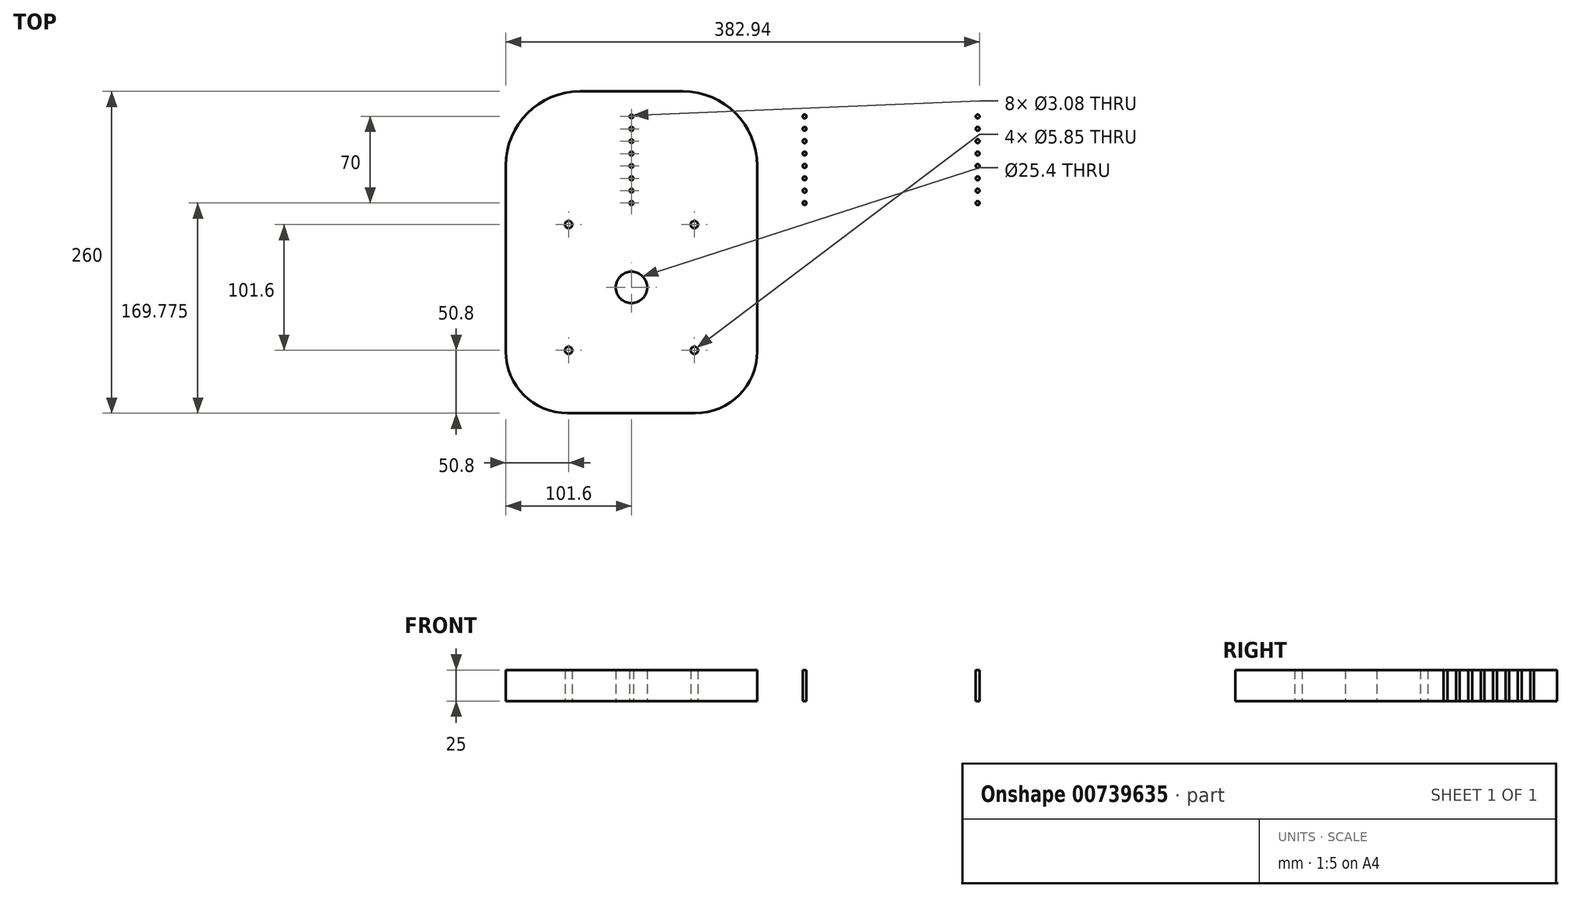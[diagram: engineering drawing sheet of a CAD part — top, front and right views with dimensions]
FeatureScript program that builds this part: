
annotation { "Feature Type Name" : "Feature", "Feature Type Description" : "" }
export const myFeature = defineFeature(function(context is Context, id is Id, definition is map)
    precondition{}
    {
        {
            var Q0;
            Q0=qCreatedBy(makeId("Top.planeOp"),FACE);
            var sketch = newSketch(context, id + "F0", { "sketchPlane" : qUnion([Q0])});
            skLineSegment(sketch, "E0.bottom", {"start": v(0, 0) * mm, "end": v(203.2, 0) * mm});
            skLineSegment(sketch, "E0.top", {"start": v(0, 260) * mm, "end": v(203.2, 260) * mm});
            skLineSegment(sketch, "E0.left", {"start": v(0, 0) * mm, "end": v(0, 260) * mm});
            skLineSegment(sketch, "E0.right", {"start": v(203.2, 0) * mm, "end": v(203.2, 260) * mm});
            skLineSegment(sketch, "E1", {"start": v(101.6, 0) * mm, "end": v(101.6, 260) * mm, "construction": true});
            skCircle(sketch, "E2", {"center": v(101.6, 239.78) * mm, "radius": 1.54 * mm});
            skCircle(sketch, "E3", {"center": v(101.6, 101.6) * mm, "radius": 12.7 * mm});
            skLineSegment(sketch, "E4.bottom", {"start": v(152.4, 152.4) * mm, "end": v(50.8, 152.4) * mm});
            skLineSegment(sketch, "E4.top", {"start": v(152.4, 50.8) * mm, "end": v(50.8, 50.8) * mm});
            skLineSegment(sketch, "E4.left", {"start": v(152.4, 152.4) * mm, "end": v(152.4, 50.8) * mm});
            skLineSegment(sketch, "E4.right", {"start": v(50.8, 152.4) * mm, "end": v(50.8, 50.8) * mm});
            skCircle(sketch, "E5", {"center": v(50.8, 152.4) * mm, "radius": 2.93 * mm});
            skCircle(sketch, "E6", {"center": v(152.4, 152.4) * mm, "radius": 2.93 * mm});
            skCircle(sketch, "E7", {"center": v(50.8, 50.8) * mm, "radius": 2.93 * mm});
            skCircle(sketch, "E8", {"center": v(152.4, 50.8) * mm, "radius": 2.93 * mm});
            skCircle(sketch, "E9.0.1.0", {"center": v(101.6, 229.78) * mm, "radius": 1.54 * mm});
            skCircle(sketch, "E9.0.2.0", {"center": v(101.6, 219.78) * mm, "radius": 1.54 * mm});
            skCircle(sketch, "E9.0.3.0", {"center": v(101.6, 209.77) * mm, "radius": 1.54 * mm});
            skCircle(sketch, "E9.0.4.0", {"center": v(101.6, 199.77) * mm, "radius": 1.54 * mm});
            skCircle(sketch, "E9.0.5.0", {"center": v(101.6, 189.77) * mm, "radius": 1.54 * mm});
            skCircle(sketch, "E9.0.6.0", {"center": v(101.6, 179.77) * mm, "radius": 1.54 * mm});
            skCircle(sketch, "E9.0.7.0", {"center": v(101.6, 169.77) * mm, "radius": 1.54 * mm});
            skCircle(sketch, "E9.1.0.0", {"center": v(241.5, 239.78) * mm, "radius": 1.54 * mm});
            skCircle(sketch, "E9.1.1.0", {"center": v(241.5, 229.78) * mm, "radius": 1.54 * mm});
            skCircle(sketch, "E9.1.2.0", {"center": v(241.5, 219.78) * mm, "radius": 1.54 * mm});
            skCircle(sketch, "E9.1.3.0", {"center": v(241.5, 209.77) * mm, "radius": 1.54 * mm});
            skCircle(sketch, "E9.1.4.0", {"center": v(241.5, 199.77) * mm, "radius": 1.54 * mm});
            skCircle(sketch, "E9.1.5.0", {"center": v(241.5, 189.77) * mm, "radius": 1.54 * mm});
            skCircle(sketch, "E9.1.6.0", {"center": v(241.5, 179.77) * mm, "radius": 1.54 * mm});
            skCircle(sketch, "E9.1.7.0", {"center": v(241.5, 169.77) * mm, "radius": 1.54 * mm});
            skCircle(sketch, "E9.2.0.0", {"center": v(381.4, 239.78) * mm, "radius": 1.54 * mm});
            skCircle(sketch, "E9.2.1.0", {"center": v(381.4, 229.78) * mm, "radius": 1.54 * mm});
            skCircle(sketch, "E9.2.2.0", {"center": v(381.4, 219.78) * mm, "radius": 1.54 * mm});
            skCircle(sketch, "E9.2.3.0", {"center": v(381.4, 209.77) * mm, "radius": 1.54 * mm});
            skCircle(sketch, "E9.2.4.0", {"center": v(381.4, 199.77) * mm, "radius": 1.54 * mm});
            skCircle(sketch, "E9.2.5.0", {"center": v(381.4, 189.77) * mm, "radius": 1.54 * mm});
            skCircle(sketch, "E9.2.6.0", {"center": v(381.4, 179.77) * mm, "radius": 1.54 * mm});
            skCircle(sketch, "E9.2.7.0", {"center": v(381.4, 169.77) * mm, "radius": 1.54 * mm});
            skLineSegment(sketch, "E9.direction1", {"start": v(101.6, 219.78) * mm, "end": v(241.5, 219.78) * mm, "construction": true});
            skLineSegment(sketch, "E9.direction2", {"start": v(101.6, 219.78) * mm, "end": v(101.6, 209.78) * mm, "construction": true});
            skSolve(sketch);
        }
        {
            var Q0;
            Q0=qSketchRegion(id+"F0",true);
            var Q1;
            Q1=makeQuery(id+"F0.imprint","IMPRINT",FACE,{"disambiguationData":[TD([[makeQuery(id+"F0.imprint","IMPRINT",EDGE,{"derivedFrom":sQuery(id+"F0.wireOp",EDGE,"E3")}),-1.0]])]});
            extrude(context, id + "F1", {"entities" : qUnion([Q0, Q1]), "depth" : 25 * mm, "offsetDistance" : 25 * mm});
        }
        {
            var Q0;
            Q0=makeQuery(id+"F1.opExtrude","SWEPT_EDGE",EDGE,{"disambiguationData":[OSD([sQuery(id+"F0.wireOp",EDGE,"E0.top"),sQuery(id+"F0.wireOp",EDGE,"E0.right")])]});
            var Q1;
            Q1=makeQuery(id+"F1.opExtrude","SWEPT_EDGE",EDGE,{"disambiguationData":[OSD([sQuery(id+"F0.wireOp",EDGE,"E0.top"),sQuery(id+"F0.wireOp",EDGE,"E0.left")])]});
            fillet(context, id + "F2", {"entities" : qUnion([Q0, Q1]), "radius" : 60 * mm, "tangentPropagation" : true, "allowEdgeOverflow" : false});
        }
        {
            var Q0;
            Q0=makeQuery(id+"F1.opExtrude","SWEPT_EDGE",EDGE,{"disambiguationData":[OSD([sQuery(id+"F0.wireOp",EDGE,"E0.bottom"),sQuery(id+"F0.wireOp",EDGE,"E0.right")])]});
            var Q1;
            Q1=makeQuery(id+"F1.opExtrude","SWEPT_EDGE",EDGE,{"disambiguationData":[OSD([sQuery(id+"F0.wireOp",EDGE,"E0.bottom"),sQuery(id+"F0.wireOp",EDGE,"E0.left")])]});
            fillet(context, id + "F3", {"entities" : qUnion([Q0, Q1]), "radius" : 50 * mm, "tangentPropagation" : true, "allowEdgeOverflow" : false});
        }
    });
